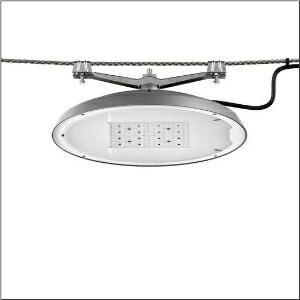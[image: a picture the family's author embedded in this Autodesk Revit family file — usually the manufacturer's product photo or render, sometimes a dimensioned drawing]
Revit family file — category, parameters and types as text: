
# Revit family: dl_50_iq_mini___st1_0s_5xa248w31f08le_9893
name_source: partatom
category: Lighting Fixtures
units: mm (PartAtom-declared; Revit-internal decimal feet)

## family parameters
Cut with Voids When Loaded = No
Host = Face
Light Source = No
Part Type = Normal
Room Calculation Point = No
Round Connector Dimension = Use Diameter
Shared = No

## types (1)
- --- (1 x LED, 10390 lm, 67.4 W, 3000K)
    Apparent Load = 67 VA
    CIE Flux Codes = 37 72 97 100 100
    Color Rendering = 70
    Color Temperature = 3000K
    Default Elevation = 1800 mm
    Description = DL 50 iQ mini, catenary luminaire, primary light control with lens, of PMMA, primary optical cover: cover, of toughened safety glass, transparent, light distribution: ST1.0s, light emission: direct distribution, primary light characteristic: symmetric, installation type: suspended mounting, LED, High Power LED, rated luminous flux: 10.390lm, luminous efficacy: 154lm/W, light colour: 730, colour temperature: 3000K, control gear: iQ Street-Remote, control: optimised constant luminous flux control (CLO 2.0), Desk-Remote (wireless, voltage-free reading and setting of iQ features in the workshop via application-optimized NFC function/RFID function), Light-Fading, Smart-Wire, Night-Set, Lumen-Switch, Temp-Guard, Auto-Match, Street-Remote, mains connection: 230..240V, AC, 50/60Hz, start of lifetime: 67W, end of service life: 70W, reduction: 31W, luminaire housing, of diecast aluminium, powder-coated, SITECO metallic grey (DB 702S), diameter: 500mm, height: 115mm, mounting height: 4..12m, protection rating (complete): IP66, insulation class (complete): insulation class II (safety insulation), certification: CE, ENEC, ENEC+, VDE, impact resistance: IK08, permissible operating ambient temperature for outdoor applications: -25..+40°C, standard-compliant lighting for roads and squares, packaging unit: 1 piece

Light Distribution: ST1.0s
    Height = 124 mm  [stored 0.406824 ft]
    Lamp = 1 x LED
    Lamp Light Flux = 10390 lm
    Lamp Power = 67.4 W
    Lamp count = 1
    Length = 500 mm
    Luminous efficacy = 154 lm/W
    Manufacturer = Siteco
    ModVariant = No
    Model = 5XA248W31F08LE
    Number of Poles = 1
    OnlyDefault = Yes
    Power Factor = 1
    Product Name = DL 50 iQ mini | ST1.0s
    Product group = catenary luminaire
    ProductGroupID = 6300
    Protection Class = Protection class II
    Protection Degree = IP 66
    RLX_Detail_Level = 1
    RLX_Emergency_Light_Flux = 0 lm
    RLX_Emergency_Type = 0
    RLX_Emergency_Type_DB = No
    RlxData = <blob elided: 126793 chars, md5=de4fd39d>
    Socket = socket
    Standby Power = 0 W
    System Light Flux = 10390 lm
    System Power = 67 W
    Type Comments = factory setting: luminous flux: 100 % | dim-lin: 254 | 705 mA
    Type Image = l_1251783.jpg
    URL = http://relux.com
    VarID = @adj_140021
    Voltage = 0 V
    Weight = 0.00 kg
    Width = 0 mm  [stored 0 ft]

note: [stored X ft] marks values corroborated as IEEE doubles in the binary element streams (Revit-internal decimal feet)

## geometry (parser evidence)
native form markers: Blend x4, Sweep x14
no freeform markers — native parametric forms only
